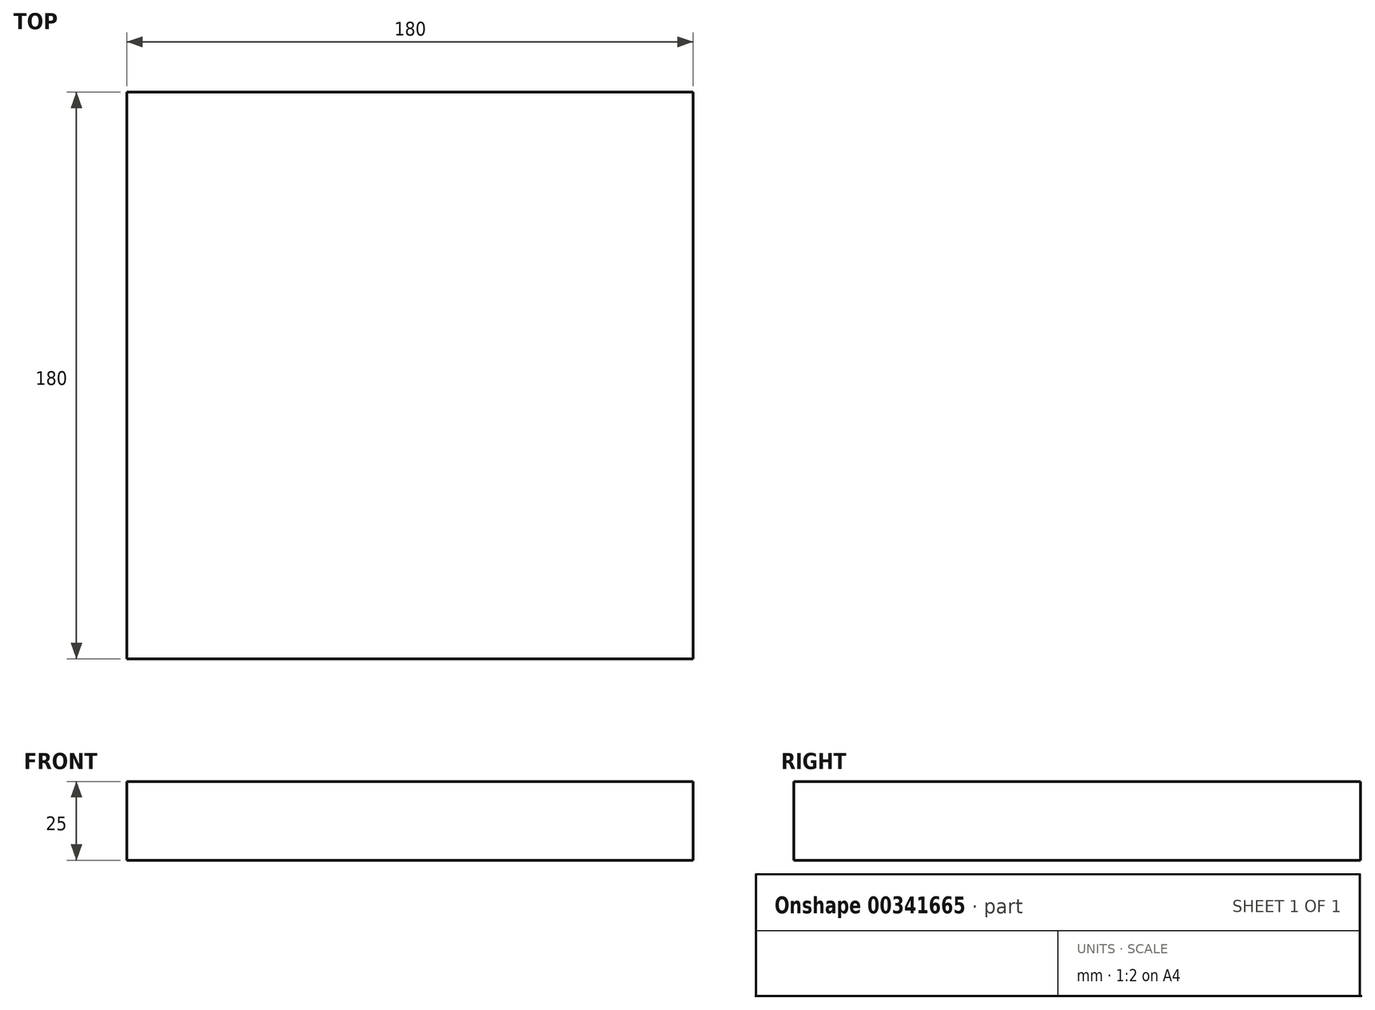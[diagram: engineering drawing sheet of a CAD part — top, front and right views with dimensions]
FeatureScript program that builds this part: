
annotation { "Feature Type Name" : "Feature", "Feature Type Description" : "" }
export const myFeature = defineFeature(function(context is Context, id is Id, definition is map)
    precondition{}
    {
        {
            var Q0;
            Q0=qCreatedBy(makeId("Top.planeOp"),FACE);
            var sketch = newSketch(context, id + "F0", { "sketchPlane" : qUnion([Q0])});
            skLineSegment(sketch, "E0.bottom", {"start": v(90, -90) * mm, "end": v(-90, -90) * mm});
            skLineSegment(sketch, "E0.top", {"start": v(90, 90) * mm, "end": v(-90, 90) * mm});
            skLineSegment(sketch, "E0.left", {"start": v(90, -90) * mm, "end": v(90, 90) * mm});
            skLineSegment(sketch, "E0.right", {"start": v(-90, -90) * mm, "end": v(-90, 90) * mm});
            skPoint(sketch, "E0.middle", {"position": v(0, 0) * mm});
            skSolve(sketch);
        }
        {
            var Q0;
            Q0 = qSketchRegion(id + "F0", true);
            extrude(context, id + "F1", {"entities" : qUnion([Q0]), "depth" : 25 * mm});
        }
    });
